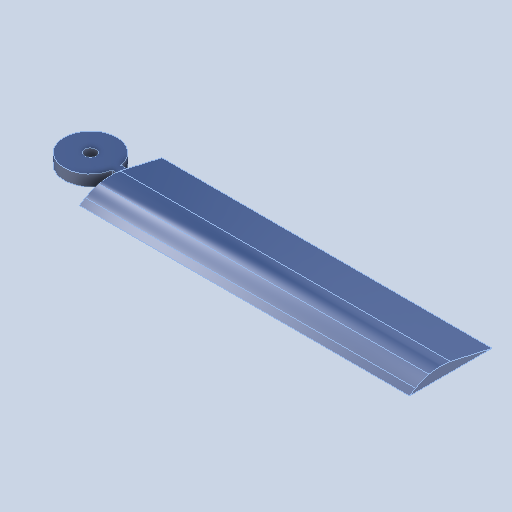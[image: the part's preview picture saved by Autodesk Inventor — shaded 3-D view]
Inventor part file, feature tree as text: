
AUTODESK INVENTOR PART (.ipt)
format: ipt  version: 2023 (Build 270158000, 158)  size: 130,560 bytes
history: native  units: mm
features: sketch x4, other x3
ambient origin geometry x8: Origin, YZ Plane, XZ Plane, XY Plane, X Axis, Y Axis, Z Axis, Center Point
bodies: Solid1 (feature_tree)
feature tree (7):
  other  "elevator"
  other  "Solid1::elevator"
  other  "TaggingFeature1"
  sketch  "Sketch1"  dims[d0=10.0mm]
  sketch  "Sketch2"
  sketch  "Sketch3"
  sketch  "Sketch4"
